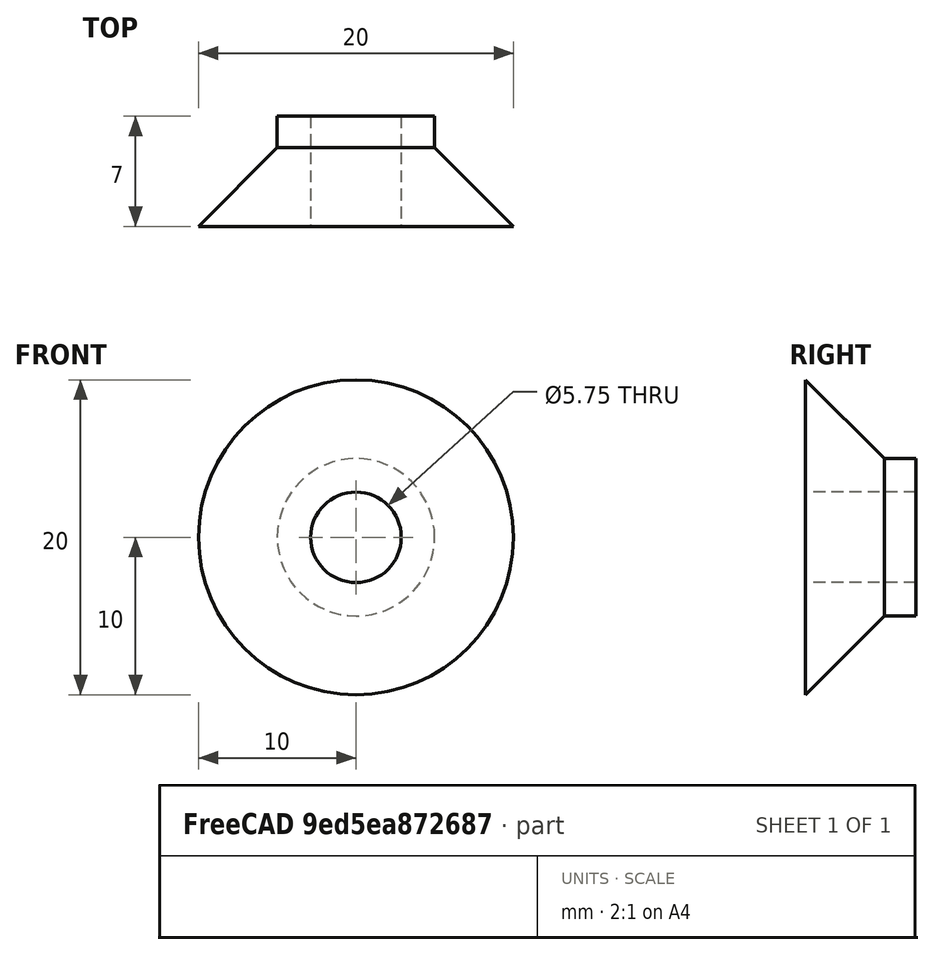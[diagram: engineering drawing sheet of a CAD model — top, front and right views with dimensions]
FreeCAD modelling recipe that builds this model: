
FCSTD DOCUMENT  (FreeCAD 0.19R24291 (Git))
Label: FDM-0009_roller-spacer
License: All rights reserved
LicenseURL: http://en.wikipedia.org/wiki/All_rights_reserved
objects: PartDesign::Plane×2, Sketcher::SketchObject×1, PartDesign::Revolution×1, Part::Part2DObjectPython×1, PartDesign::Body×1
note: 7 computed .brp shape members not serialized (recipe doc carries the construction recipe); baked Part::Feature solids carry a one-line shape summary decoded from their .brp

FEATURE [Sketcher::SketchObject] Sketch
  FullyConstrained = true
  MapMode = 5
  Support = -> [XY_Plane]
  sketch-geometry (5):
    g0: LineSegment StartX=-2.875 StartY=0 StartZ=0 EndX=-10 EndY=0 EndZ=0
    g1: LineSegment StartX=-10 StartY=0 StartZ=0 EndX=-5 EndY=5 EndZ=0
    g2: LineSegment StartX=-5 StartY=5 StartZ=0 EndX=-5 EndY=7 EndZ=0
    g3: LineSegment StartX=-5 StartY=7 StartZ=0 EndX=-2.875 EndY=7 EndZ=0
    g4: LineSegment StartX=-2.875 StartY=7 StartZ=0 EndX=-2.875 EndY=0 EndZ=0
  constraints (15):
    c: PointOnObject(g0,g-1)
    c: PointOnObject(g0,g-1)
    c: Coincident(g0,g1)
    c: Coincident(g1,g2)
    c: Vertical(g2)
    c: Coincident(g2,g3)
    c: Horizontal(g3)
    c: Coincident(g3,g4)
    c: Coincident(g4,g0)
    c: Vertical(g4)
    c: Distance(g-1,g4) = 2.875
    c: DistanceY(g4,g4) = 7
    c: Distance(g2,g-2) = 5
    c: Angle(g2,g1) = 2.35619
    c: DistanceY(g-1,g1) = 5
FEATURE [PartDesign::Revolution] Revolution
  AllowMultiFace = false
  Angle = 360
  Axis = (0,1,0)
  Base = (0,0,0)
  Profile = -> Sketch
  ReferenceAxis = -> Sketch [V_Axis]
FEATURE [PartDesign::Plane] DatumPlane  label="Datum"
  Length = 73.5482
  MapMode = 5
  Placement = pos=(0,0,0) rot=(1,0,0;1.5708rad)
  ResizeMode = 0
  Support = -> [Revolution]
  Width = 61.1695
FEATURE [Part::Part2DObjectPython] ShapeString  label="PN"  # Draft 2D object (typed FeaturePython)
  FontFile = ../../lib/fonts/RobotoMono-VariableFont_weight.ttf
  MapMode = 5
  Placement = pos=(0,0,0) rot=(1,0,0;1.5708rad)
  Size = 5
  String = FDM-0009-00
  Support = -> [XZ_Plane]
  Tracking = 0
FEATURE [PartDesign::Plane] DatumPlane001  label="PrintPlane"
  Length = 73.5482
  MapMode = 5
  Placement = pos=(0,0,0) rot=(1,0,0;1.5708rad)
  ResizeMode = 0
  Support = -> [Revolution]
  Width = 61.1695
FEATURE [PartDesign::Body] Body
  Group = -> [Sketch,Revolution,DatumPlane,ShapeString,DatumPlane001]
  Origin = -> Origin
  Tip = -> Revolution
